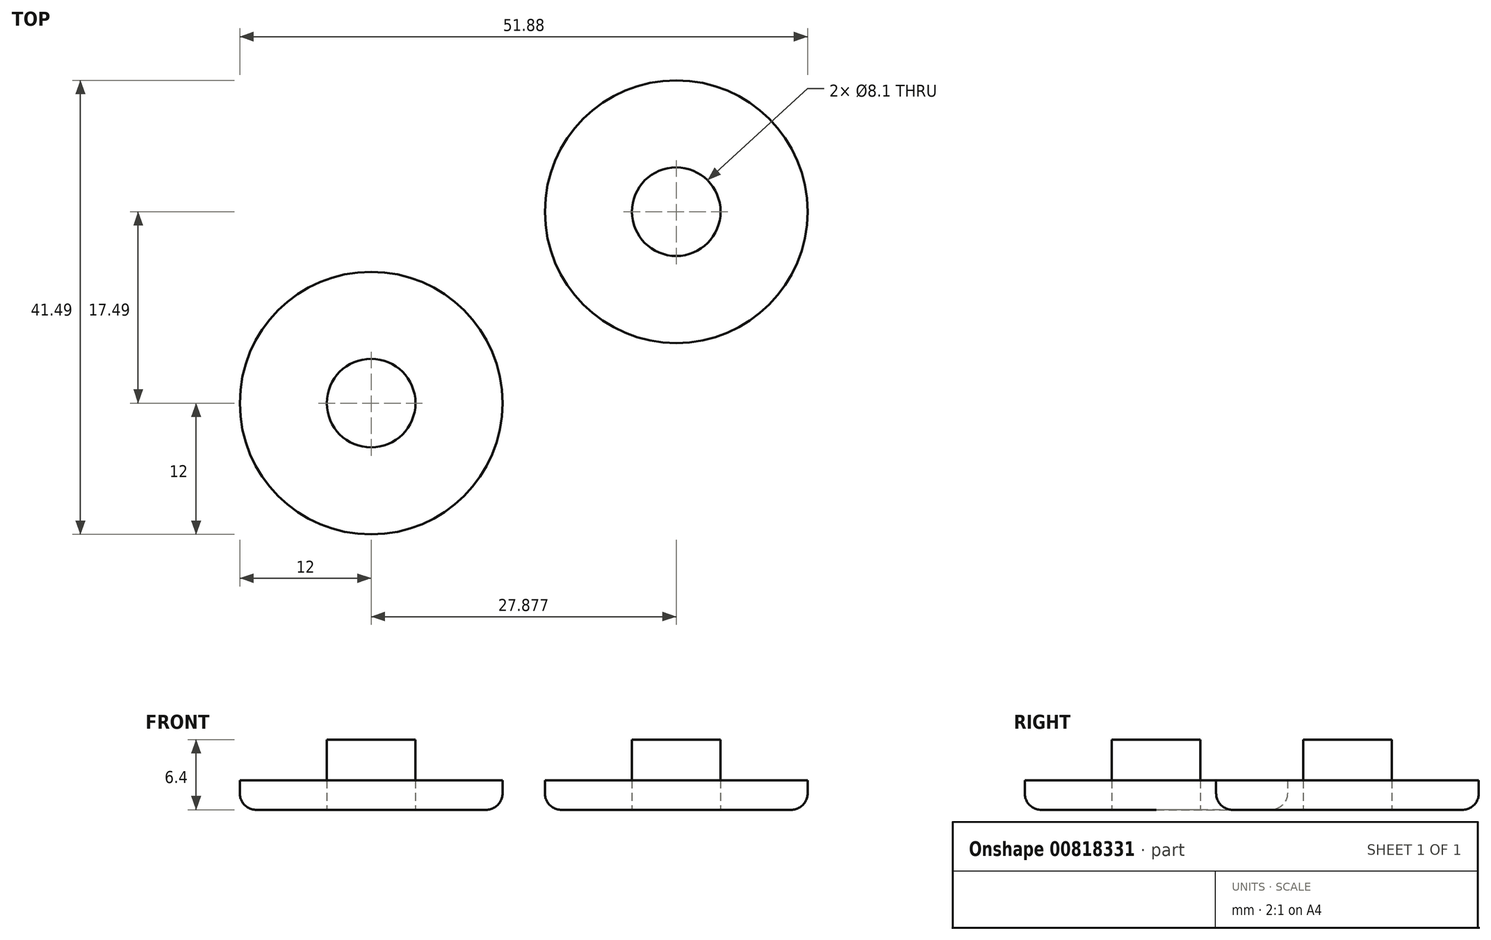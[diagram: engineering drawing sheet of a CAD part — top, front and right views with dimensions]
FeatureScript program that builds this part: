
annotation { "Feature Type Name" : "Feature", "Feature Type Description" : "" }
export const myFeature = defineFeature(function(context is Context, id is Id, definition is map)
    precondition{}
    {
        {
            var Q0;
            Q0=qCreatedBy(makeId("Top.planeOp"),FACE);
            var sketch = newSketch(context, id + "F0", { "sketchPlane" : qUnion([Q0])});
            skCircle(sketch, "E0", {"center": v(0, 0) * mm, "radius": 12 * mm});
            skCircle(sketch, "E1", {"center": v(0, 0) * mm, "radius": 4.05 * mm});
            skCircle(sketch, "E2", {"center": v(27.88, 17.49) * mm, "radius": 12 * mm});
            skCircle(sketch, "E3", {"center": v(27.88, 17.49) * mm, "radius": 4.05 * mm});
            skSolve(sketch);
        }
        {
            var Q0;
            Q0 = qSketchRegion(id + "F0", true);
            extrude(context, id + "F1", {"entities" : qUnion([Q0]), "depth" : 2.7 * mm, "offsetDistance" : 25 * mm});
        }
        {
            var Q0;
            Q0=makeQuery(id+"F0.imprint","IMPRINT",FACE,{"disambiguationData":[TD([[makeQuery(id+"F0.imprint","IMPRINT",EDGE,{"derivedFrom":sQuery(id+"F0.wireOp",EDGE,"E1")}),1.0]])]});
            var Q1;
            Q1=makeQuery(id+"F0.imprint","IMPRINT",FACE,{"disambiguationData":[TD([[makeQuery(id+"F0.imprint","IMPRINT",EDGE,{"derivedFrom":sQuery(id+"F0.wireOp",EDGE,"E3")}),1.0]])]});
            extrude(context, id + "F2", {"entities" : qUnion([Q0, Q1]), "depth" : 6.4 * mm, "offsetDistance" : 25 * mm});
        }
        {
            var Q0;
            Q0=makeQuery(id+"F1.opExtrude","CAP_EDGE",EDGE,{"disambiguationData":[OSD([sQuery(id+"F0.wireOp",EDGE,"E2")])],"isStart":true});
            var Q1;
            Q1=makeQuery(id+"F1.opExtrude","CAP_EDGE",EDGE,{"disambiguationData":[OSD([sQuery(id+"F0.wireOp",EDGE,"E0")])],"isStart":true});
            fillet(context, id + "F3", {"entities" : qUnion([Q0, Q1]), "radius" : 1.5 * mm, "tangentPropagation" : true, "allowEdgeOverflow" : false});
        }
    });
